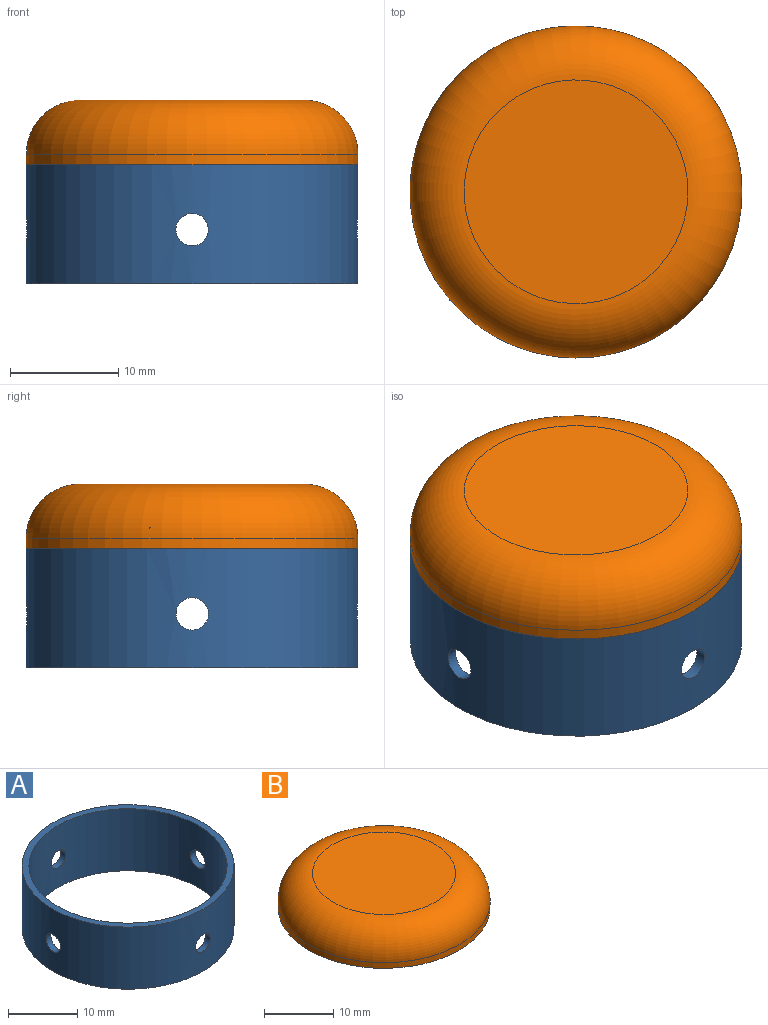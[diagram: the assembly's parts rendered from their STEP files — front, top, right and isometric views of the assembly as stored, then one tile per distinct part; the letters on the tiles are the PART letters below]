
ASSEMBLY  parts=2 mates=1
PART A: 8 faces, bbox 30.7x30.7x11 mm
  f0: cylinder r=14.35mm len=28.7mm, axis (0,0,-1), area 963.5mm2, adj f2,f3,f4,f5,f6,f7
  f1: cylinder r=15.35mm len=30.7mm, axis (0,0,-1), area 1032.6mm2, adj f2,f3,f4,f5,f6,f7
  f2: plane 30.7x30.7mm, normal (0,0,1), area 93.3mm2, adj f0,f1
  f3: plane 30.7x30.7mm, normal (0,0,-1), area 93.3mm2, adj f0,f1
  f4: cylinder r=1.5mm len=3mm, axis (1,0,0), area 9.4mm2, adj f0,f1
  f5: cylinder r=1.5mm len=3mm, axis (1,0,0), area 9.4mm2, adj f0,f1
  f6: cylinder r=1.5mm len=3mm, axis (0,-1,0), area 9.4mm2, adj f0,f1
  f7: cylinder r=1.5mm len=3mm, axis (0,-1,0), area 9.4mm2, adj f0,f1
PART B: 88 faces, bbox 33.2x33.2x6 mm
  f0: plane 30.7x30.7mm, normal (0,0,-1), area 362.2mm2, adj f1,f3,f4,f5,f6,f7,f8,f10
  f1: cylinder r=15.35mm len=30.7mm, axis (0,0,1), area 96.4mm2, adj f0,f87
  f2: plane 20.7x20.7mm, normal (0,0,1), area 336.5mm2, adj f87
  f3: plane 3.35x2mm, normal (1,0,0), area 6.7mm2, adj f0,f4,f8,f9
  f4: plane 2.91x2mm, normal (0.5,0.87,0), area 6.7mm2, adj f0,f3,f5,f9
  f5: plane 3.02x2mm, normal (-0.5,0.87,0), area 7mm2, adj f0,f4,f6,f9
  f6: plane 3.35x2mm, normal (-1,0,0), area 6.7mm2, adj f0,f5,f7,f9
  f7: plane 2.91x2mm, normal (-0.5,-0.87,0), area 6.7mm2, adj f0,f6,f8,f9
  f8: plane 3.02x2mm, normal (0.5,-0.87,0), area 7mm2, adj f0,f3,f7,f9
  f9: plane 6.77x5.93mm, normal (0,0,-1), area 30mm2, adj f3,f4,f5,f6,f7,f8
  f10: plane 3.02x2mm, normal (-0.5,0.87,0), area 7mm2, adj f0,f11,f15,f16
  f11: plane 3.49x2mm, normal (-1,0,0), area 7mm2, adj f0,f10,f12,f16
  f12: plane 3.02x2mm, normal (-0.5,-0.87,0), area 7mm2, adj f0,f11,f13,f16
  f13: plane 3.02x2mm, normal (0.5,-0.87,0), area 7mm2, adj f0,f12,f14,f16
  f14: plane 3.49x2mm, normal (1,0,0), area 7mm2, adj f0,f13,f15,f16
  f15: plane 3.02x2mm, normal (0.5,0.87,0), area 7mm2, adj f0,f10,f14,f16
  f16: plane 6.98x6.04mm, normal (0,0,-1), area 31.6mm2, adj f10,f11,f12,f13,f14,f15
  f17: plane 3.02x2mm, normal (0.5,0.87,0), area 7mm2, adj f0,f18,f22,f23
  f18: plane 3.02x2mm, normal (-0.5,0.87,0), area 7mm2, adj f0,f17,f19,f23
  f19: plane 3.49x2mm, normal (-1,0,0), area 7mm2, adj f0,f18,f20,f23
  f20: plane 3.02x2mm, normal (-0.5,-0.87,0), area 7mm2, adj f0,f19,f21,f23
  f21: plane 3.02x2mm, normal (0.5,-0.87,0), area 7mm2, adj f0,f20,f22,f23
  f22: plane 3.49x2mm, normal (1,0,0), area 7mm2, adj f0,f17,f21,f23
  f23: plane 6.98x6.04mm, normal (0,0,-1), area 31.6mm2, adj f17,f18,f19,f20,f21,f22
  f24: plane 3.02x2mm, normal (0.5,0.87,0), area 7mm2, adj f0,f25,f29,f30
  f25: plane 3.02x2mm, normal (-0.5,0.87,0), area 7mm2, adj f0,f24,f26,f30
  f26: plane 3.49x2mm, normal (-1,0,0), area 7mm2, adj f0,f25,f27,f30
  f27: plane 3.02x2mm, normal (-0.5,-0.87,0), area 7mm2, adj f0,f26,f28,f30
  f28: plane 3.02x2mm, normal (0.5,-0.87,0), area 7mm2, adj f0,f27,f29,f30
  f29: plane 3.49x2mm, normal (1,0,0), area 7mm2, adj f0,f24,f28,f30
  f30: plane 6.98x6.04mm, normal (0,0,-1), area 31.6mm2, adj f24,f25,f26,f27,f28,f29
  f31: plane 3.49x2mm, normal (-1,0,0), area 7mm2, adj f0,f32,f36,f37
  f32: plane 3.02x2mm, normal (-0.5,-0.87,0), area 7mm2, adj f0,f31,f33,f37
  f33: plane 3.02x2mm, normal (0.5,-0.87,0), area 7mm2, adj f0,f32,f34,f37
  f34: plane 3.49x2mm, normal (1,0,0), area 7mm2, adj f0,f33,f35,f37
  f35: plane 3.02x2mm, normal (0.5,0.87,0), area 7mm2, adj f0,f34,f36,f37
  f36: plane 3.02x2mm, normal (-0.5,0.87,0), area 7mm2, adj f0,f31,f35,f37
  f37: plane 6.98x6.04mm, normal (0,0,-1), area 31.6mm2, adj f31,f32,f33,f34,f35,f36
  f38: plane 3.02x2mm, normal (0.5,0.87,0), area 7mm2, adj f0,f39,f43,f44
  f39: plane 3.02x2mm, normal (-0.5,0.87,0), area 7mm2, adj f0,f38,f40,f44
  f40: plane 3.49x2mm, normal (-1,0,0), area 7mm2, adj f0,f39,f41,f44
  f41: plane 3.02x2mm, normal (-0.5,-0.87,0), area 7mm2, adj f0,f40,f42,f44
  f42: plane 3.02x2mm, normal (0.5,-0.87,0), area 7mm2, adj f0,f41,f43,f44
  f43: plane 3.49x2mm, normal (1,0,0), area 7mm2, adj f0,f38,f42,f44
  f44: plane 6.98x6.04mm, normal (0,0,-1), area 31.6mm2, adj f38,f39,f40,f41,f42,f43
  f45: plane 3.02x2mm, normal (0.5,0.87,0), area 7mm2, adj f0,f46,f50,f51
  f46: plane 3.02x2mm, normal (-0.5,0.87,0), area 7mm2, adj f0,f45,f47,f51
  f47: plane 3.49x2mm, normal (-1,0,0), area 7mm2, adj f0,f46,f48,f51
  f48: plane 3.02x2mm, normal (-0.5,-0.87,0), area 7mm2, adj f0,f47,f49,f51
  f49: plane 3.02x2mm, normal (0.5,-0.87,0), area 7mm2, adj f0,f48,f50,f51
  f50: plane 3.49x2mm, normal (1,0,0), area 7mm2, adj f0,f45,f49,f51
  f51: plane 6.98x6.04mm, normal (0,0,-1), area 31.6mm2, adj f45,f46,f47,f48,f49,f50
  f52: plane 3.02x2mm, normal (0.5,0.87,0), area 7mm2, adj f0,f53,f57,f58
  f53: plane 3.02x2mm, normal (-0.5,0.87,0), area 7mm2, adj f0,f52,f54,f58
  f54: plane 3.49x2mm, normal (-1,0,0), area 7mm2, adj f0,f53,f55,f58
  f55: plane 3.02x2mm, normal (-0.5,-0.87,0), area 7mm2, adj f0,f54,f56,f58
  f56: plane 3.02x2mm, normal (0.5,-0.87,0), area 7mm2, adj f0,f55,f57,f58
  f57: plane 3.49x2mm, normal (1,0,0), area 7mm2, adj f0,f52,f56,f58
  f58: plane 6.98x6.04mm, normal (0,0,-1), area 31.6mm2, adj f52,f53,f54,f55,f56,f57
  f59: plane 3.02x2mm, normal (0.5,0.87,0), area 7mm2, adj f0,f60,f64,f65
  f60: plane 3.02x2mm, normal (-0.5,0.87,0), area 7mm2, adj f0,f59,f61,f65
  f61: plane 3.49x2mm, normal (-1,0,0), area 7mm2, adj f0,f60,f62,f65
  f62: plane 3.02x2mm, normal (-0.5,-0.87,0), area 7mm2, adj f0,f61,f63,f65
  f63: plane 3.02x2mm, normal (0.5,-0.87,0), area 7mm2, adj f0,f62,f64,f65
  f64: plane 3.49x2mm, normal (1,0,0), area 7mm2, adj f0,f59,f63,f65
  f65: plane 6.98x6.04mm, normal (0,0,-1), area 31.6mm2, adj f59,f60,f61,f62,f63,f64
  f66: plane 3.02x2mm, normal (0.5,0.87,0), area 7mm2, adj f0,f67,f71,f72
  f67: plane 3.02x2mm, normal (-0.5,0.87,0), area 7mm2, adj f0,f66,f68,f72
  f68: plane 3.49x2mm, normal (-1,0,0), area 7mm2, adj f0,f67,f69,f72
  f69: plane 3.02x2mm, normal (-0.5,-0.87,0), area 7mm2, adj f0,f68,f70,f72
  f70: plane 3.02x2mm, normal (0.5,-0.87,0), area 7mm2, adj f0,f69,f71,f72
  f71: plane 3.49x2mm, normal (1,0,0), area 7mm2, adj f0,f66,f70,f72
  f72: plane 6.98x6.04mm, normal (0,0,-1), area 31.6mm2, adj f66,f67,f68,f69,f70,f71
  f73: plane 3.02x2mm, normal (0.5,0.87,0), area 7mm2, adj f0,f74,f78,f79
  f74: plane 3.02x2mm, normal (-0.5,0.87,0), area 7mm2, adj f0,f73,f75,f79
  f75: plane 3.49x2mm, normal (-1,0,0), area 7mm2, adj f0,f74,f76,f79
  f76: plane 3.02x2mm, normal (-0.5,-0.87,0), area 7mm2, adj f0,f75,f77,f79
  f77: plane 3.02x2mm, normal (0.5,-0.87,0), area 7mm2, adj f0,f76,f78,f79
  f78: plane 3.49x2mm, normal (1,0,0), area 7mm2, adj f0,f73,f77,f79
  f79: plane 6.98x6.04mm, normal (0,0,-1), area 31.6mm2, adj f73,f74,f75,f76,f77,f78
  f80: plane 3.02x2mm, normal (0.5,0.87,0), area 7mm2, adj f0,f81,f85,f86
  f81: plane 3.02x2mm, normal (-0.5,0.87,0), area 7mm2, adj f0,f80,f82,f86
  f82: plane 3.49x2mm, normal (-1,0,0), area 7mm2, adj f0,f81,f83,f86
  f83: plane 3.02x2mm, normal (-0.5,-0.87,0), area 7mm2, adj f0,f82,f84,f86
  f84: plane 3.02x2mm, normal (0.5,-0.87,0), area 7mm2, adj f0,f83,f85,f86
  f85: plane 3.49x2mm, normal (1,0,0), area 7mm2, adj f0,f80,f84,f86
  f86: plane 6.98x6.04mm, normal (0,0,-1), area 31.6mm2, adj f80,f81,f82,f83,f84,f85
  f87: torus R=10.35mm, axis (0,0,1), area 667.8mm2, adj f1,f2
PLACE A rot(axis=(0,0,-1),90deg) t=(0,0,-24)mm
PLACE B t=(0,0,-7)mm
MATE fastened A.f1 <-> B.f1  axis (0,0,1) through (0,0,-13)mm
